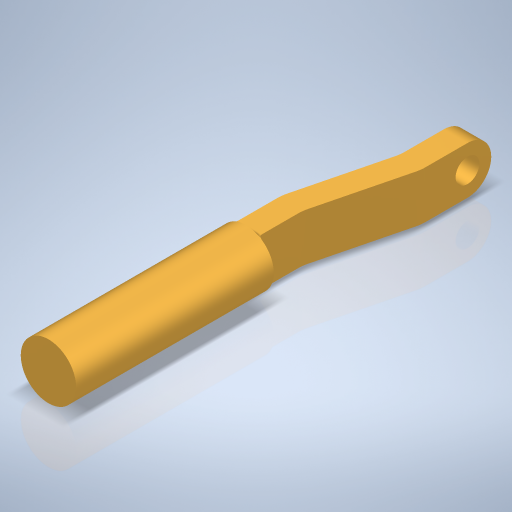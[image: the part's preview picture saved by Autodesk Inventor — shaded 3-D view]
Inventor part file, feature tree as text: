
AUTODESK INVENTOR PART (.ipt)
format: ipt  version: 2024 (Build 280153000, 153)  size: 321,024 bytes
history: native  units: mm
features: sketch x4, extrude x3, fillet x2, plane x1, hole x1
ambient origin geometry x8: Origin, YZ Plane, XZ Plane, XY Plane, X Axis, Y Axis, Z Axis, Center Point
bodies: Volumenkörper1 (feature_tree)
feature tree (11):
  extrude  "Extrusion1"  Depth=25.0mm TaperAngle=0.0deg
  plane  "Arbeitsebene1"
  extrude  "Extrusion2"  Depth=2.0mm
  extrude  "Extrusion3"  Depth=31.0mm
  fillet  "Rundung1"  Radius=43.0mm
  hole  "Bohrung1"  [1 undecoded]
  fillet  "Rundung2"  Radius=6.0mm
  sketch  "Skizze1"  dims[d0=7.0mm d1=25.0mm d2=0.0mm]
  sketch  "Skizze2"  dims[d3=0.0mm d4=2.0mm]
  sketch  "Skizze3"  dims[d6=3.0mm d7=31.0mm d8=43.0mm]
  sketch  "Skizze4"  dims[d9=3.0mm d10=48.5mm d11=6.0mm d12=0.0mm d13=6.0mm d14=0.0mm d15=4.5mm d16=3.0mm d17=6.0mm d18=4.0mm d19=2.0mm d20=90.0deg d21=8.0mm d22=0.0mm d23=0.5mm]
note: 1 required parameter value undecoded (feature->parameter linkage not recoverable at this tier; creation-order binding heuristic only, values carry confidence <= 0.55)
